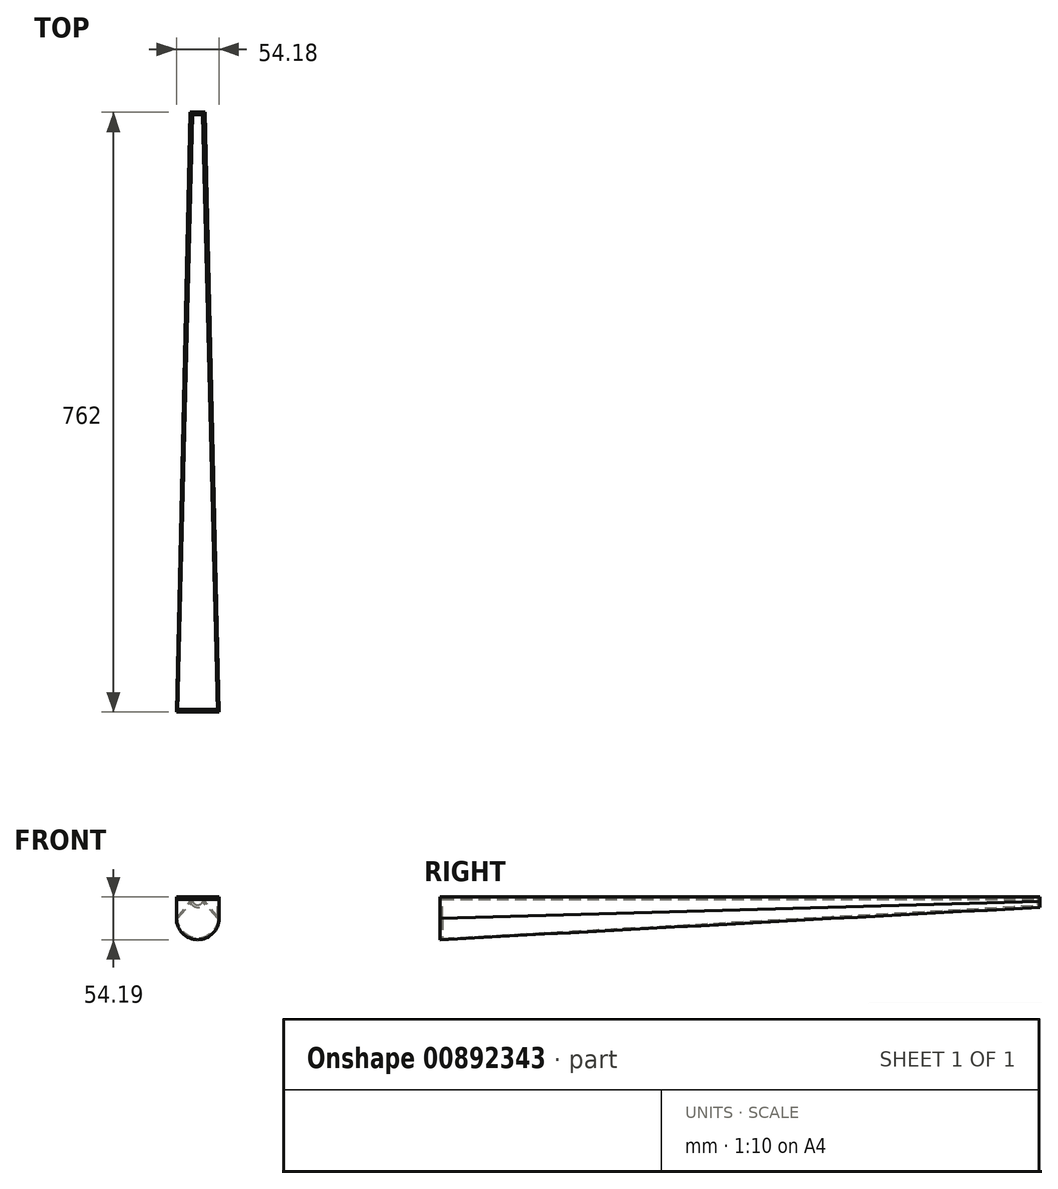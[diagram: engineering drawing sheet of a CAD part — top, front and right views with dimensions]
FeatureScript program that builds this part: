
annotation { "Feature Type Name" : "Feature", "Feature Type Description" : "" }
export const myFeature = defineFeature(function(context is Context, id is Id, definition is map)
    precondition{}
    {
        {
            var Q0;
            Q0=qCreatedBy(makeId("Front.planeOp"),FACE);
            var sketch = newSketch(context, id + "F0", { "sketchPlane" : qUnion([Q0])});
            skLineSegment(sketch, "E0.left", {"start": v(27.1, -13.55) * mm, "end": v(27.1, 13.55) * mm});
            skLineSegment(sketch, "E0.right", {"start": v(-27.1, -13.55) * mm, "end": v(-27.1, 13.55) * mm});
            skPoint(sketch, "E0.middle", {"position": v(0, 0) * mm});
            skArc(sketch, "E1", {"start": v(-27.1, -13.55) * mm, "mid": v(0, -40.64) * mm, "end": v(27.1, -13.55) * mm});
            skLineSegment(sketch, "E2", {"start": v(-27.1, 13.55) * mm, "end": v(-25.4, 13.55) * mm});
            skArc(sketch, "E3.0", {"start": v(-25.4, -13.55) * mm, "mid": v(0, -38.95) * mm, "end": v(25.4, -13.55) * mm});
            skLineSegment(sketch, "E4.trimOffspring", {"start": v(25.4, 13.55) * mm, "end": v(27.1, 13.55) * mm});
            skLineSegment(sketch, "E5", {"start": v(-25.4, 13.55) * mm, "end": v(-25.4, 10.34) * mm});
            skLineSegment(sketch, "E6", {"start": v(25.4, 13.55) * mm, "end": v(25.4, 10.34) * mm});
            skLineSegment(sketch, "E7", {"start": v(25.4, 10.34) * mm, "end": v(-25.4, 10.34) * mm});
            skLineSegment(sketch, "E8", {"start": v(-25.4, 10.34) * mm, "end": v(-25.4, -13.55) * mm});
            skLineSegment(sketch, "E9", {"start": v(25.4, 10.34) * mm, "end": v(25.4, -13.55) * mm});
            skLineSegment(sketch, "E10", {"start": v(-25.4, 10.34) * mm, "end": v(-27.1, 10.34) * mm});
            skLineSegment(sketch, "E11", {"start": v(25.4, 10.34) * mm, "end": v(27.1, 10.34) * mm});
            skSolve(sketch);
        }
        {
            var Q0;
            Q0=makeQuery(id+"F0.imprint","IMPRINT",FACE,{"disambiguationData":[TD([[makeQuery(id+"F0.imprint","IMPRINT",EDGE,{"derivedFrom":sQuery(id+"F0.wireOp",EDGE,"E3.0")}),1.0]])]});
            extrude(context, id + "F1", {"entities" : qUnion([Q0]), "oppositeDirection" : true, "depth" : 3.17 * mm, "offsetDistance" : 25.4 * mm});
        }
        {
            var Q0;
            Q0=makeQuery(id+"F0.imprint","IMPRINT",FACE,{"disambiguationData":[TD([[makeQuery(id+"F0.imprint","IMPRINT",EDGE,{"derivedFrom":sQuery(id+"F0.wireOp",EDGE,"E0.left")}),1.0]])]});
            cPlane(context, id + "F2", {"entities" : qUnion([Q0]), "cplaneType" : CPlaneType.OFFSET, "offset" : 762 * mm, "oppositeDirection" : true, "width" : 152.4 * mm, "height" : 152.4 * mm});
        }
        {
            var Q0;
            Q0=qCreatedBy(id+"F2.planeOp",FACE);
            var sketch = newSketch(context, id + "F3", { "sketchPlane" : qUnion([Q0])});
            skLineSegment(sketch, "E12", {"start": v(-9.52, 13.55) * mm, "end": v(-6.35, 13.55) * mm});
            skLineSegment(sketch, "E13.trimOffspring", {"start": v(6.35, 13.55) * mm, "end": v(9.52, 13.55) * mm});
            skLineSegment(sketch, "E14", {"start": v(9.52, 13.55) * mm, "end": v(9.52, 7.8) * mm});
            skLineSegment(sketch, "E15", {"start": v(-6.35, 13.55) * mm, "end": v(-6.35, 7.8) * mm});
            skLineSegment(sketch, "E16", {"start": v(-9.52, 13.55) * mm, "end": v(-9.52, 7.8) * mm});
            skArc(sketch, "E17", {"start": v(-6.35, 7.8) * mm, "mid": v(0, 3.5) * mm, "end": v(6.35, 7.8) * mm});
            skArc(sketch, "E18", {"start": v(-9.52, 7.8) * mm, "mid": v(0, 0.48) * mm, "end": v(9.52, 7.8) * mm});
            skLineSegment(sketch, "E19", {"start": v(6.35, 13.55) * mm, "end": v(6.35, 10.34) * mm});
            skLineSegment(sketch, "E20", {"start": v(6.35, 10.34) * mm, "end": v(6.35, 7.8) * mm});
            skLineSegment(sketch, "E21", {"start": v(6.35, 10.34) * mm, "end": v(-6.35, 10.34) * mm});
            skLineSegment(sketch, "E22", {"start": v(6.35, 10.34) * mm, "end": v(9.52, 10.34) * mm});
            skLineSegment(sketch, "E23", {"start": v(-6.35, 10.34) * mm, "end": v(-9.52, 10.34) * mm});
            skSolve(sketch);
        }
        {
            var Q1;
            {var subQ0=sQuery(id+"F0.wireOp",EDGE,"E1");Q1=makeQuery(id+"F0.imprint","IMPRINT",FACE,{"disambiguationData":[TD([[makeQuery(id+"F0.imprint","IMPRINT",EDGE,{"derivedFrom":subQ0}),1.0]])]});}
            var Q2;
            {var subQ3=sQuery(id+"F3.wireOp",EDGE,"E17");Q2=makeQuery(id+"F3.imprint","IMPRINT",FACE,{"disambiguationData":[TD([[makeQuery(id+"F3.imprint","IMPRINT",EDGE,{"derivedFrom":subQ3}),-1.0]])]});}
            loft(context, id + "F4", {"sheetProfilesArray" : [{ "sheetProfileEntities" : qUnion([Q1]) }, { "sheetProfileEntities" : qUnion([Q2]) }]});
        }
        {
            var Q1;
            {var subQ0=sQuery(id+"F0.wireOp",EDGE,"E2");Q1=makeQuery(id+"F0.imprint","IMPRINT",FACE,{"disambiguationData":[TD([[makeQuery(id+"F0.imprint","IMPRINT",EDGE,{"derivedFrom":subQ0}),-1.0]])]});}
            var Q2;
            {var subQ0=sQuery(id+"F3.wireOp",EDGE,"E12");Q2=makeQuery(id+"F3.imprint","IMPRINT",FACE,{"disambiguationData":[TD([[makeQuery(id+"F3.imprint","IMPRINT",EDGE,{"derivedFrom":subQ0}),-1.0]])]});}
            loft(context, id + "F5", {"operationType" : NewBodyOperationType.ADD, "sheetProfilesArray" : [{ "sheetProfileEntities" : qUnion([Q1]) }, { "sheetProfileEntities" : qUnion([Q2]) }]});
        }
        {
            var Q1;
            {var subQ0=sQuery(id+"F0.wireOp",EDGE,"E4.trimOffspring");Q1=makeQuery(id+"F0.imprint","IMPRINT",FACE,{"disambiguationData":[TD([[makeQuery(id+"F0.imprint","IMPRINT",EDGE,{"derivedFrom":subQ0}),-1.0]])]});}
            var Q2;
            {var subQ0=sQuery(id+"F3.wireOp",EDGE,"E13.trimOffspring");Q2=makeQuery(id+"F3.imprint","IMPRINT",FACE,{"disambiguationData":[TD([[makeQuery(id+"F3.imprint","IMPRINT",EDGE,{"derivedFrom":subQ0}),-1.0]])]});}
            loft(context, id + "F6", {"operationType" : NewBodyOperationType.ADD, "sheetProfilesArray" : [{ "sheetProfileEntities" : qUnion([Q1]) }, { "sheetProfileEntities" : qUnion([Q2]) }]});
        }
        {
            var Q0;
            {var subQ0=sQuery(id+"F3.wireOp",EDGE,"E17");Q0=makeQuery(id+"F3.imprint","IMPRINT",FACE,{"disambiguationData":[TD([[makeQuery(id+"F3.imprint","IMPRINT",EDGE,{"derivedFrom":subQ0}),1.0]])]});}
            extrude(context, id + "F7", {"entities" : qUnion([Q0]), "depth" : 3.17 * mm, "offsetDistance" : 25.4 * mm});
        }
        {
            var Q0;
            Q0=makeQuery(id+"F7.opExtrude","SWEPT_FACE",FACE,{"disambiguationData":[OSD([sQuery(id+"F3.wireOp",EDGE,"E21")])]});
            extrude(context, id + "F8", {"entities" : qUnion([Q0]), "depth" : 3.17 * mm, "offsetDistance" : 25.4 * mm});
        }
        {
            var Q0;
            Q0=makeQuery(id+"F1.opExtrude","SWEPT_FACE",FACE,{"disambiguationData":[OSD([sQuery(id+"F0.wireOp",EDGE,"E7")])]});
            extrude(context, id + "F9", {"entities" : qUnion([Q0]), "depth" : 3.17 * mm, "offsetDistance" : 25.4 * mm});
        }
        {
            var Q0;
            {var subQ0=sQuery(id+"F0.wireOp",EDGE,"E7");Q0=makeQuery(id+"F9.opExtrude","SWEPT_FACE",FACE,{"disambiguationData":[OSD([subQ0]),TDD([makeQuery(id+"F1.opExtrude","CAP_EDGE",EDGE,{"disambiguationData":[OSD([subQ0])],"isStart":false})])]});}
            var Q1;
            {var subQ0=sQuery(id+"F3.wireOp",EDGE,"E21");Q1=makeQuery(id+"F8.opExtrude","SWEPT_FACE",FACE,{"disambiguationData":[OSD([subQ0]),TDD([makeQuery(id+"F7.opExtrude","CAP_EDGE",EDGE,{"disambiguationData":[OSD([subQ0])],"isStart":false})])]});}
            loft(context, id + "F10", {"sheetProfilesArray" : [{ "sheetProfileEntities" : qUnion([Q0]) }, { "sheetProfileEntities" : qUnion([Q1]) }]});
        }
    });
